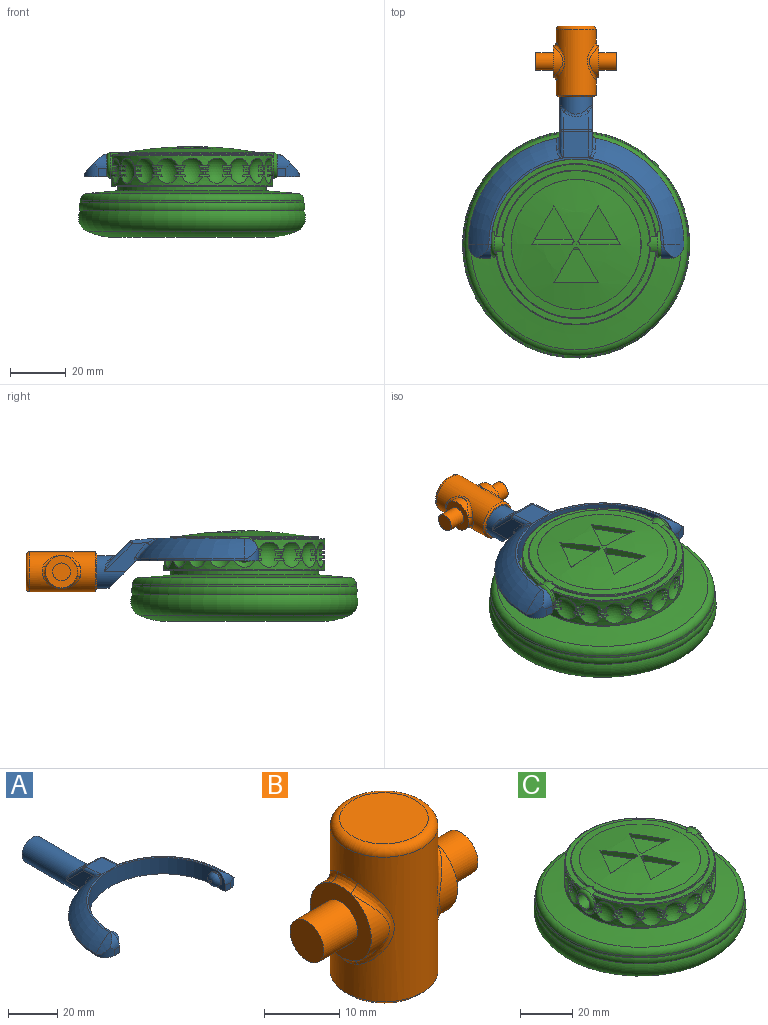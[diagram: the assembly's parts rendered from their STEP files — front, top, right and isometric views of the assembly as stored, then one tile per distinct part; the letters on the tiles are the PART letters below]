
ASSEMBLY  parts=3 mates=2
PART A: 48 faces, bbox 77.3x80.8x18.2 mm
  f0: plane 11.99x9.83mm, normal (0,-0.71,-0.71), area 141.5mm2, adj f1,f2,f9,f30,f43,f46
  f1: plane 15.39x10.49mm, normal (-1,0,0), area 63.5mm2, adj f0,f30,f32,f36,f46,f47
  f2: plane 15.39x10.49mm, normal (1,0,0), area 63.5mm2, adj f0,f30,f34,f39,f43,f44
  f3: plane 9.14x6.37mm, normal (0,0.71,0.71), area 67.6mm2, adj f35,f36,f39,f40
  f4: cylinder r=38.61mm len=37.99mm, axis (0,0,-1), area 42.6mm2, adj f6,f9,f17,f46,f47
  f5: torus R=19.3mm, axis (0,0,-1), area 507.8mm2, adj f10,f11,f12,f29,f42,f44
  f6: torus R=19.3mm, axis (0,0,-1), area 507.8mm2, adj f4,f11,f15,f28,f45,f47
  f7: cylinder r=30.48mm len=60.96mm, axis (0,0,-1), area 746.6mm2, adj f8,f9,f11,f14,f21,f24
  f8: plane 8.13x5.08mm, normal (-1,0,0), area 19.9mm2, adj f7,f9,f13,f19,f24
  f9: plane 77.22x43.73mm, normal (0,0,-1), area 956.2mm2, adj f0,f4,f7,f8,f10,f13,f14,f16
  f10: cylinder r=38.61mm len=37.99mm, axis (0,0,-1), area 42.6mm2, adj f5,f9,f20,f43,f44
  f11: plane 62.55x30.95mm, normal (0,0,1), area 75mm2, adj f5,f6,f7,f18,f19,f27
  f12: cylinder r=22.71mm len=7.33mm, axis (0,1,0), area 24.8mm2, adj f5,f19,f20
  f13: plane 3.05x3.05mm, normal (0,-1,0), area 9.3mm2, adj f8,f9,f19,f20
  f14: plane 8.13x5.08mm, normal (1,0,0), area 19.9mm2, adj f7,f9,f16,f18,f21
  f15: cylinder r=22.71mm len=7.33mm, axis (0,1,0), area 24.8mm2, adj f6,f17,f18
  f16: plane 3.05x3.05mm, normal (0,-1,0), area 9.3mm2, adj f9,f14,f17,f18
  f17: cylinder r=5.08mm len=5.08mm, axis (0,0,-1), area 21.9mm2, adj f4,f9,f15,f16,f18
  f18: cylinder r=5.08mm len=5.08mm, axis (-1,0,0), area 21.9mm2, adj f11,f14,f15,f16,f17
  f19: cylinder r=5.08mm len=5.08mm, axis (-1,0,0), area 21.9mm2, adj f8,f11,f12,f13,f20
  f20: cylinder r=5.08mm len=5.08mm, axis (0,0,-1), area 21.9mm2, adj f9,f10,f12,f13,f19
  f21: cylinder r=3.17mm len=6.35mm, axis (-1,0,0), area 12.7mm2, adj f7,f14,f23
  f22: plane 1.27x1.27mm, normal (1,0,0), area 1.3mm2, adj f23
  f23: torus R=0.64mm, axis (1,0,0), area 56.5mm2, adj f21,f22
  f24: cylinder r=3.17mm len=6.35mm, axis (1,0,0), area 12.7mm2, adj f7,f8,f26
  f25: plane 1.27x1.27mm, normal (-1,0,0), area 1.3mm2, adj f26
  f26: torus R=0.64mm, axis (-1,0,0), area 56.5mm2, adj f24,f25
  f27: plane 9.86x9.36mm, normal (0,0.09,1), area 85.6mm2, adj f11,f28,f29,f32,f34,f35,f42,f45
  f28: plane 1.04x0.17mm, normal (0,-1,0), area 0mm2, adj f6,f27,f45
  f29: plane 1.04x0.17mm, normal (0,-1,0), area 0mm2, adj f5,f27,f42
  f30: cylinder r=5.84mm len=33.01mm, axis (0,-1,0), area 1029.7mm2, adj f0,f1,f2,f31,f38,f40,f41
  f31: plane 11.68x11.68mm, normal (0,1,0), area 107.2mm2, adj f30
  f32: cylinder r=1.27mm len=9.13mm, axis (0,-1,0.09), area 14.4mm2, adj f1,f27,f33,f45
  f33: sphere r=1.27mm, area 1.5mm2, adj f32,f35,f36
  f34: cylinder r=1.27mm len=9.13mm, axis (0,1,-0.09), area 14.4mm2, adj f2,f27,f37,f42
  f35: cylinder r=1.27mm len=9.14mm, axis (-1,0,0), area 8.1mm2, adj f3,f27,f33,f37
  f36: cylinder r=1.27mm len=10.91mm, axis (0,-0.71,0.71), area 23.1mm2, adj f1,f3,f33,f38
  f37: sphere r=1.27mm, area 1.5mm2, adj f34,f35,f39
  f38: bspline ~4.55x2.75mm, area 2.3mm2, adj f30,f36,f40
  f39: cylinder r=1.27mm len=10.91mm, axis (0,0.71,-0.71), area 23.1mm2, adj f2,f3,f37,f41
  f40: bspline ~9.14x2.56mm, area 10.7mm2, adj f3,f30,f38,f41
  f41: bspline ~5.23x3.53mm, area 2.3mm2, adj f30,f39,f40
  f42: bspline ~4.62x3.14mm, area 5.2mm2, adj f5,f27,f29,f34,f44
  f43: cylinder r=1.27mm len=1.74mm, axis (0,0,-1), area 1.9mm2, adj f0,f2,f9,f10,f44
  f44: bspline ~8.6x7.86mm, area 11.9mm2, adj f2,f5,f10,f42,f43
  f45: bspline ~4.62x3.14mm, area 5.2mm2, adj f6,f27,f28,f32,f47
  f46: cylinder r=1.27mm len=1.74mm, axis (0,0,-1), area 1.9mm2, adj f0,f1,f4,f9,f47
  f47: bspline ~8.6x7.86mm, area 11.9mm2, adj f1,f4,f6,f45,f46
PART B: 25 faces, bbox 28.9x15.5x25.4 mm
  f0: cylinder r=5.71mm len=10.81mm, axis (-1,0,0), area 26.2mm2, adj f5,f15
  f1: cylinder r=5.71mm len=10.81mm, axis (-1,0,0), area 26.2mm2, adj f8,f11
  f2: cylinder r=7.14mm len=23.5mm, axis (0,0,-1), area 763.2mm2, adj f9,f10,f11,f12,f13,f14,f15,f16
  f3: plane 11.75x11.75mm, normal (0,0,1), area 108.4mm2, adj f17
  f4: plane 13.02x13.02mm, normal (0,0,-1), area 16.3mm2, adj f22,f24
  f5: plane 11.46x11.46mm, normal (1,0,0), area 70.9mm2, adj f0,f6,f13,f16,f18
  f6: cylinder r=5.71mm len=10.81mm, axis (-1,0,0), area 26.2mm2, adj f5,f14
  f7: cylinder r=5.71mm len=10.81mm, axis (-1,0,0), area 26.2mm2, adj f8,f10
  f8: plane 11.46x11.46mm, normal (-1,0,0), area 70.9mm2, adj f1,f7,f9,f12,f20
  f9: bspline ~4.64x1.73mm, area 6.5mm2, adj f2,f8,f10,f11
  f10: bspline ~13.62x4.91mm, area 20.7mm2, adj f2,f7,f9,f12
  f11: bspline ~13.6x4.87mm, area 20.7mm2, adj f1,f2,f9,f12
  f12: bspline ~4.64x1.73mm, area 6.5mm2, adj f2,f8,f10,f11
  f13: bspline ~4.64x1.73mm, area 6.5mm2, adj f2,f5,f14,f15
  f14: bspline ~13.62x4.91mm, area 20.7mm2, adj f2,f6,f13,f16
  f15: bspline ~13.6x4.87mm, area 20.7mm2, adj f0,f2,f13,f16
  f16: bspline ~4.64x1.73mm, area 6.5mm2, adj f2,f5,f14,f15
  f17: torus R=5.87mm, axis (0,0,1), area 83.8mm2, adj f2,f3
  f18: cylinder r=3.17mm len=6.35mm, axis (-1,0,0), area 126.7mm2, adj f5,f19
  f19: plane 6.35x6.35mm, normal (1,0,0), area 31.7mm2, adj f18
  f20: cylinder r=3.17mm len=6.35mm, axis (1,0,0), area 126.7mm2, adj f8,f21
  f21: plane 6.35x6.35mm, normal (-1,0,0), area 31.7mm2, adj f20
  f22: cylinder r=6.1mm len=22.86mm, axis (0,0,-1), area 875.6mm2, adj f4,f23
  f23: plane 12.19x12.19mm, normal (0,0,-1), area 116.7mm2, adj f22
  f24: cone r=7.14mm half-angle=45deg, axis (0,0,1), area 38.5mm2, adj f2,f4
PART C: 294 faces, bbox 96.3x96.3x32.5 mm
  f0: sphere r=5.62mm, area 0.7mm2, adj f45,f49,f106,f282
  f1: sphere r=5.62mm, area 15.9mm2, adj f39,f48,f125,f282
  f2: sphere r=5.62mm, area 0.7mm2, adj f36,f40,f105,f282
  f3: cylinder r=28.87mm len=57.43mm, axis (0,0,-1), area 156mm2, adj f34,f43,f71,f72,f73,f74,f75,f76
  f4: cylinder r=28.87mm len=57.43mm, axis (0,0,-1), area 156mm2, adj f31,f52,f62,f63,f64,f65,f66,f67
  f5: cylinder r=28.87mm len=0.95mm, axis (0,0,-1), area 0.4mm2, adj f17,f33,f79,f283
  f6: cylinder r=28.87mm len=0.95mm, axis (0,0,-1), area 0.4mm2, adj f35,f42,f71,f282
  f7: cylinder r=28.87mm len=0.95mm, axis (0,0,-1), area 0.4mm2, adj f44,f51,f70,f282
  f8: cylinder r=28.87mm len=0.95mm, axis (0,0,-1), area 0.4mm2, adj f21,f30,f62,f283
  f9: sphere r=5.62mm, area 0.7mm2, adj f18,f28,f96,f283
  f10: sphere r=5.62mm, area 15.9mm2, adj f24,f27,f125,f283
  f11: sphere r=5.62mm, area 0.7mm2, adj f20,f25,f115,f283
  f12: plane 56.98x25.96mm, normal (0,0,1), area 166.4mm2, adj f15,f282,f283,f288
  f13: plane 56.98x25.96mm, normal (0,0,1), area 166.4mm2, adj f14,f282,f283,f291
  f14: cylinder r=26.57mm len=53.04mm, axis (0,0,-1), area 43.8mm2, adj f13,f282,f283,f292
  f15: cylinder r=26.57mm len=53.04mm, axis (0,0,-1), area 43.8mm2, adj f12,f282,f283,f289
  f16: cone r=26.57mm half-angle=87deg, axis (0,0,-1), area 474.1mm2, adj f282,f283,f289,f292,f293
  f17: plane 1.55x1.41mm, normal (0,0,-1), area 1.2mm2, adj f5,f19,f79,f283
  f18: plane 1.71x1.55mm, normal (0,0,1), area 1.5mm2, adj f9,f19,f79,f96,f283
  f19: cylinder r=27.6mm len=1.71mm, axis (0,0,-1), area 1mm2, adj f17,f18,f79,f283
  f20: plane 1.71x1.55mm, normal (0,0,1), area 1.5mm2, adj f11,f22,f62,f115,f283
  f21: plane 1.55x1.41mm, normal (0,0,-1), area 1.2mm2, adj f8,f22,f62,f283
  f22: cylinder r=27.6mm len=1.71mm, axis (0,0,-1), area 1mm2, adj f20,f21,f62,f283
  f23: cylinder r=27.6mm len=3.74mm, axis (0,0,-1), area 2.1mm2, adj f24,f25,f62,f283
  f24: plane 3.74x1.73mm, normal (0,0,1), area 3.1mm2, adj f10,f23,f62,f125,f283
  f25: plane 2.64x1.63mm, normal (0,0,-1), area 2.3mm2, adj f11,f23,f62,f115,f283
  f26: cylinder r=27.6mm len=3.74mm, axis (0,0,-1), area 2.1mm2, adj f27,f28,f79,f283
  f27: plane 3.74x1.73mm, normal (0,0,1), area 3.1mm2, adj f10,f26,f79,f125,f283
  f28: plane 2.64x1.63mm, normal (0,0,-1), area 2.3mm2, adj f9,f26,f79,f96,f283
  f29: cylinder r=27.6mm len=1.73mm, axis (0,0,-1), area 1mm2, adj f30,f31,f62,f283
  f30: plane 1.56x1.4mm, normal (0,0,1), area 1.1mm2, adj f8,f29,f62,f283
  f31: plane 1.68x1.62mm, normal (0,0,-1), area 1.4mm2, adj f4,f29,f62,f283
  f32: cylinder r=27.6mm len=1.73mm, axis (0,0,-1), area 1mm2, adj f33,f34,f79,f283
  f33: plane 1.56x1.4mm, normal (0,0,1), area 1.1mm2, adj f5,f32,f79,f283
  f34: plane 1.68x1.62mm, normal (0,0,-1), area 1.4mm2, adj f3,f32,f79,f283
  f35: plane 1.55x1.41mm, normal (0,0,-1), area 1.2mm2, adj f6,f37,f71,f282
  f36: plane 1.71x1.55mm, normal (0,0,1), area 1.5mm2, adj f2,f37,f71,f105,f282
  f37: cylinder r=27.6mm len=1.71mm, axis (0,0,-1), area 1mm2, adj f35,f36,f71,f282
  f38: cylinder r=27.6mm len=3.74mm, axis (0,0,-1), area 2.1mm2, adj f39,f40,f71,f282
  f39: plane 3.74x1.73mm, normal (0,0,1), area 3.1mm2, adj f1,f38,f71,f125,f282
  f40: plane 2.64x1.63mm, normal (0,0,-1), area 2.3mm2, adj f2,f38,f71,f105,f282
  f41: cylinder r=27.6mm len=1.73mm, axis (0,0,-1), area 1mm2, adj f42,f43,f71,f282
  f42: plane 1.56x1.4mm, normal (0,0,1), area 1.1mm2, adj f6,f41,f71,f282
  f43: plane 1.68x1.62mm, normal (0,0,-1), area 1.4mm2, adj f3,f41,f71,f282
  f44: plane 1.55x1.41mm, normal (0,0,-1), area 1.2mm2, adj f7,f46,f70,f282
  f45: plane 1.71x1.55mm, normal (0,0,1), area 1.5mm2, adj f0,f46,f70,f106,f282
  f46: cylinder r=27.6mm len=1.71mm, axis (0,0,-1), area 1mm2, adj f44,f45,f70,f282
  f47: cylinder r=27.6mm len=3.74mm, axis (0,0,-1), area 2.1mm2, adj f48,f49,f70,f282
  f48: plane 3.74x1.73mm, normal (0,0,1), area 3.1mm2, adj f1,f47,f70,f125,f282
  f49: plane 2.64x1.63mm, normal (0,0,-1), area 2.3mm2, adj f0,f47,f70,f106,f282
  f50: cylinder r=27.6mm len=1.73mm, axis (0,0,-1), area 1mm2, adj f51,f52,f70,f282
  f51: plane 1.56x1.4mm, normal (0,0,1), area 1.1mm2, adj f7,f50,f70,f282
  f52: plane 1.68x1.62mm, normal (0,0,-1), area 1.4mm2, adj f4,f50,f70,f282
  f53: cylinder r=1.27mm len=2.26mm, axis (0,0,1), area 2.9mm2, adj f54,f61,f272,f280
  f54: plane 14.61x2.12mm, normal (0,1,0), area 26.2mm2, adj f53,f61,f271,f280
  f55: plane 13.69x11.86mm, normal (0,0,1), area 81.2mm2, adj f271,f272,f280
  f56: plane 14.61x2.12mm, normal (0,1,0), area 26.2mm2, adj f57,f61,f274,f279
  f57: cylinder r=1.27mm len=2.26mm, axis (0,0,1), area 2.9mm2, adj f56,f61,f273,f279
  f58: plane 13.69x11.86mm, normal (0,0,1), area 81.2mm2, adj f273,f274,f279
  f59: cylinder r=1.27mm len=2.26mm, axis (0,0,1), area 3mm2, adj f61,f276,f277,f278
  f60: plane 15.88x11.86mm, normal (0,0,1), area 107.1mm2, adj f275,f276,f277,f278
  f61: sphere r=135.39mm, area 1385.3mm2, adj f53,f54,f56,f57,f59,f271,f272,f273
  f62: sphere r=5.62mm, area 66.8mm2, adj f4,f8,f20,f21,f22,f23,f24,f25
  f63: sphere r=5.62mm, area 66.8mm2, adj f4,f94,f95,f113,f114,f125,f253,f254
  f64: sphere r=5.62mm, area 66.8mm2, adj f4,f93,f94,f112,f113,f125,f244,f245
  f65: sphere r=5.62mm, area 66.8mm2, adj f4,f92,f93,f111,f112,f125,f235,f236
  f66: sphere r=5.62mm, area 66.8mm2, adj f4,f91,f92,f110,f111,f125,f226,f227
  f67: sphere r=5.62mm, area 66.8mm2, adj f4,f90,f91,f109,f110,f125,f217,f218
  f68: sphere r=5.62mm, area 66.8mm2, adj f4,f89,f90,f108,f109,f125,f208,f209
  f69: sphere r=5.62mm, area 66.8mm2, adj f4,f88,f89,f107,f108,f125,f199,f200
  f70: sphere r=5.62mm, area 66.8mm2, adj f4,f7,f44,f45,f46,f47,f48,f49
  f71: sphere r=5.62mm, area 66.8mm2, adj f3,f6,f35,f36,f37,f38,f39,f40
  f72: sphere r=5.62mm, area 66.8mm2, adj f3,f86,f87,f103,f104,f125,f181,f182
  f73: sphere r=5.62mm, area 66.8mm2, adj f3,f85,f86,f102,f103,f125,f172,f173
  f74: sphere r=5.62mm, area 66.8mm2, adj f3,f84,f85,f101,f102,f125,f163,f164
  f75: sphere r=5.62mm, area 66.8mm2, adj f3,f83,f84,f100,f101,f125,f154,f155
  f76: sphere r=5.62mm, area 66.8mm2, adj f3,f82,f83,f99,f100,f125,f145,f146
  f77: sphere r=5.62mm, area 66.8mm2, adj f3,f81,f82,f98,f99,f125,f136,f137
  f78: sphere r=5.62mm, area 66.8mm2, adj f3,f80,f81,f97,f98,f125,f127,f128
  f79: sphere r=5.62mm, area 66.8mm2, adj f3,f5,f17,f18,f19,f26,f27,f28
  f80: cylinder r=28.87mm len=0.95mm, axis (0,0,-1), area 0.7mm2, adj f78,f79,f127,f134
  f81: cylinder r=28.87mm len=0.95mm, axis (0,0,-1), area 0.7mm2, adj f77,f78,f136,f143
  f82: cylinder r=28.87mm len=0.95mm, axis (0,0,-1), area 0.7mm2, adj f76,f77,f145,f152
  f83: cylinder r=28.87mm len=0.95mm, axis (0,0,-1), area 0.7mm2, adj f75,f76,f154,f161
  f84: cylinder r=28.87mm len=0.95mm, axis (0,0,-1), area 0.7mm2, adj f74,f75,f163,f170
  f85: cylinder r=28.87mm len=0.95mm, axis (0,0,-1), area 0.7mm2, adj f73,f74,f172,f179
  f86: cylinder r=28.87mm len=0.95mm, axis (0,0,-1), area 0.7mm2, adj f72,f73,f181,f188
  f87: cylinder r=28.87mm len=0.95mm, axis (0,0,-1), area 0.7mm2, adj f71,f72,f190,f197
  f88: cylinder r=28.87mm len=0.95mm, axis (0,0,-1), area 0.7mm2, adj f69,f70,f199,f206
  f89: cylinder r=28.87mm len=0.95mm, axis (0,0,-1), area 0.7mm2, adj f68,f69,f208,f215
  f90: cylinder r=28.87mm len=0.95mm, axis (0,0,-1), area 0.7mm2, adj f67,f68,f217,f224
  f91: cylinder r=28.87mm len=0.95mm, axis (0,0,-1), area 0.7mm2, adj f66,f67,f226,f233
  f92: cylinder r=28.87mm len=0.95mm, axis (0,0,-1), area 0.7mm2, adj f65,f66,f235,f242
  f93: cylinder r=28.87mm len=0.95mm, axis (0,0,-1), area 0.7mm2, adj f64,f65,f244,f251
  f94: cylinder r=28.87mm len=0.95mm, axis (0,0,-1), area 0.7mm2, adj f63,f64,f253,f260
  f95: cylinder r=28.87mm len=0.95mm, axis (0,0,-1), area 0.7mm2, adj f62,f63,f263,f269
  f96: cylinder r=28.87mm len=0.95mm, axis (0,0,-1), area 0.7mm2, adj f9,f18,f28,f79
  f97: cylinder r=28.87mm len=0.95mm, axis (0,0,-1), area 0.7mm2, adj f78,f79,f128,f132
  f98: cylinder r=28.87mm len=0.95mm, axis (0,0,-1), area 0.7mm2, adj f77,f78,f137,f141
  f99: cylinder r=28.87mm len=0.95mm, axis (0,0,-1), area 0.7mm2, adj f76,f77,f146,f150
  f100: cylinder r=28.87mm len=0.95mm, axis (0,0,-1), area 0.7mm2, adj f75,f76,f155,f159
  f101: cylinder r=28.87mm len=0.95mm, axis (0,0,-1), area 0.7mm2, adj f74,f75,f164,f168
  f102: cylinder r=28.87mm len=0.95mm, axis (0,0,-1), area 0.7mm2, adj f73,f74,f173,f177
  f103: cylinder r=28.87mm len=0.95mm, axis (0,0,-1), area 0.7mm2, adj f72,f73,f182,f186
  f104: cylinder r=28.87mm len=0.95mm, axis (0,0,-1), area 0.7mm2, adj f71,f72,f191,f195
  f105: cylinder r=28.87mm len=0.95mm, axis (0,0,-1), area 0.7mm2, adj f2,f36,f40,f71
  f106: cylinder r=28.87mm len=0.95mm, axis (0,0,-1), area 0.7mm2, adj f0,f45,f49,f70
  f107: cylinder r=28.87mm len=0.95mm, axis (0,0,-1), area 0.7mm2, adj f69,f70,f200,f204
  f108: cylinder r=28.87mm len=0.95mm, axis (0,0,-1), area 0.7mm2, adj f68,f69,f209,f213
  f109: cylinder r=28.87mm len=0.95mm, axis (0,0,-1), area 0.7mm2, adj f67,f68,f218,f222
  f110: cylinder r=28.87mm len=0.95mm, axis (0,0,-1), area 0.7mm2, adj f66,f67,f227,f231
  f111: cylinder r=28.87mm len=0.95mm, axis (0,0,-1), area 0.7mm2, adj f65,f66,f236,f240
  f112: cylinder r=28.87mm len=0.95mm, axis (0,0,-1), area 0.7mm2, adj f64,f65,f245,f249
  f113: cylinder r=28.87mm len=0.95mm, axis (0,0,-1), area 0.7mm2, adj f63,f64,f254,f258
  f114: cylinder r=28.87mm len=0.95mm, axis (0,0,-1), area 0.7mm2, adj f62,f63,f264,f265
  f115: cylinder r=28.87mm len=0.95mm, axis (0,0,-1), area 0.7mm2, adj f11,f20,f25,f62
  f116: plane 39.33x39.33mm, normal (0,0,-1), area 1214.6mm2, adj f117
  f117: torus R=20.12mm, axis (0,0,-1), area 1429.3mm2, adj f116,f118
  f118: torus R=27.74mm, axis (0,0,-1), area 3542.1mm2, adj f117,f119
  f119: torus R=35.36mm, axis (0,0,-1), area 2180.1mm2, adj f118,f120
  f120: torus R=37.35mm, axis (0,0,-1), area 734.6mm2, adj f119,f121
  f121: cylinder r=40.06mm len=80.11mm, axis (0,0,-1), area 213.3mm2, adj f120,f126
  f122: cone r=26.57mm half-angle=85deg, axis (0,0,-1), area 2265mm2, adj f123,f126
  f123: cylinder r=26.57mm len=53.14mm, axis (0,0,-1), area 265mm2, adj f122,f124
  f124: plane 57.23x57.23mm, normal (0,0,-1), area 354.5mm2, adj f123,f290
  f125: cylinder r=28.87mm len=57.73mm, axis (0,0,-1), area 339.8mm2, adj f1,f10,f24,f27,f39,f48,f62,f63
  f126: torus R=37.52mm, axis (0,0,1), area 928.6mm2, adj f121,f122
  f127: plane 2.51x1.93mm, normal (0,0,-1), area 2mm2, adj f78,f79,f80,f129
  f128: plane 2.51x1.93mm, normal (0,0,1), area 2mm2, adj f78,f79,f97,f129
  f129: cylinder r=27.6mm len=2.51mm, axis (0,0,-1), area 1.8mm2, adj f78,f79,f127,f128
  f130: cylinder r=27.6mm len=3.53mm, axis (0,0,-1), area 2.3mm2, adj f78,f79,f131,f132
  f131: plane 3.53x2.4mm, normal (0,0,1), area 3.2mm2, adj f78,f79,f125,f130
  f132: plane 2.92x2.12mm, normal (0,0,-1), area 2.5mm2, adj f78,f79,f97,f130
  f133: cylinder r=27.6mm len=3.52mm, axis (0,0,-1), area 2.3mm2, adj f78,f79,f134,f135
  f134: plane 2.91x2.12mm, normal (0,0,1), area 2.5mm2, adj f78,f79,f80,f133
  f135: plane 3.52x2.39mm, normal (0,0,-1), area 3.1mm2, adj f3,f78,f79,f133
  f136: plane 2.12x2.12mm, normal (0,0,-1), area 2mm2, adj f77,f78,f81,f138
  f137: plane 2.12x2.12mm, normal (0,0,1), area 2mm2, adj f77,f78,f98,f138
  f138: cylinder r=27.6mm len=1.99mm, axis (0,0,-1), area 1.8mm2, adj f77,f78,f136,f137
  f139: cylinder r=27.6mm len=2.81mm, axis (0,0,-1), area 2.3mm2, adj f77,f78,f140,f141
  f140: plane 2.82x2.82mm, normal (0,0,1), area 3.2mm2, adj f77,f78,f125,f139
  f141: plane 2.41x2.41mm, normal (0,0,-1), area 2.5mm2, adj f77,f78,f98,f139
  f142: cylinder r=27.6mm len=2.79mm, axis (0,0,-1), area 2.3mm2, adj f77,f78,f143,f144
  f143: plane 2.4x2.4mm, normal (0,0,1), area 2.5mm2, adj f77,f78,f81,f142
  f144: plane 2.81x2.81mm, normal (0,0,-1), area 3.1mm2, adj f3,f77,f78,f142
  f145: plane 2.51x1.93mm, normal (0,0,-1), area 2mm2, adj f76,f77,f82,f147
  f146: plane 2.51x1.93mm, normal (0,0,1), area 2mm2, adj f76,f77,f99,f147
  f147: cylinder r=27.6mm len=2.51mm, axis (0,0,-1), area 1.8mm2, adj f76,f77,f145,f146
  f148: cylinder r=27.6mm len=3.53mm, axis (0,0,-1), area 2.3mm2, adj f76,f77,f149,f150
  f149: plane 3.53x2.4mm, normal (0,0,1), area 3.2mm2, adj f76,f77,f125,f148
  f150: plane 2.92x2.12mm, normal (0,0,-1), area 2.5mm2, adj f76,f77,f99,f148
  f151: cylinder r=27.6mm len=3.52mm, axis (0,0,-1), area 2.3mm2, adj f76,f77,f152,f153
  f152: plane 2.91x2.12mm, normal (0,0,1), area 2.5mm2, adj f76,f77,f82,f151
  f153: plane 3.52x2.39mm, normal (0,0,-1), area 3.1mm2, adj f3,f76,f77,f151
  f154: plane 2.78x1.55mm, normal (0,0,-1), area 2mm2, adj f75,f76,f83,f156
  f155: plane 2.78x1.55mm, normal (0,0,1), area 2mm2, adj f75,f76,f100,f156
  f156: cylinder r=27.6mm len=2.78mm, axis (0,0,-1), area 1.8mm2, adj f75,f76,f154,f155
  f157: cylinder r=27.6mm len=3.92mm, axis (0,0,-1), area 2.3mm2, adj f75,f76,f158,f159
  f158: plane 3.92x1.73mm, normal (0,0,1), area 3.2mm2, adj f75,f76,f125,f157
  f159: plane 3.24x1.63mm, normal (0,0,-1), area 2.5mm2, adj f75,f76,f100,f157
  f160: cylinder r=27.6mm len=3.9mm, axis (0,0,-1), area 2.3mm2, adj f75,f76,f161,f162
  f161: plane 3.23x1.62mm, normal (0,0,1), area 2.5mm2, adj f75,f76,f83,f160
  f162: plane 3.9x1.73mm, normal (0,0,-1), area 3.1mm2, adj f3,f75,f76,f160
  f163: plane 2.78x1.55mm, normal (0,0,-1), area 2mm2, adj f74,f75,f84,f165
  f164: plane 2.78x1.55mm, normal (0,0,1), area 2mm2, adj f74,f75,f101,f165
  f165: cylinder r=27.6mm len=2.78mm, axis (0,0,-1), area 1.8mm2, adj f74,f75,f163,f164
  f166: cylinder r=27.6mm len=3.92mm, axis (0,0,-1), area 2.3mm2, adj f74,f75,f167,f168
  f167: plane 3.92x1.73mm, normal (0,0,1), area 3.2mm2, adj f74,f75,f125,f166
  f168: plane 3.24x1.63mm, normal (0,0,-1), area 2.5mm2, adj f74,f75,f101,f166
  f169: cylinder r=27.6mm len=3.9mm, axis (0,0,-1), area 2.3mm2, adj f74,f75,f170,f171
  f170: plane 3.23x1.62mm, normal (0,0,1), area 2.5mm2, adj f74,f75,f84,f169
  f171: plane 3.9x1.73mm, normal (0,0,-1), area 3.1mm2, adj f3,f74,f75,f169
  f172: plane 2.51x1.93mm, normal (0,0,-1), area 2mm2, adj f73,f74,f85,f174
  f173: plane 2.51x1.93mm, normal (0,0,1), area 2mm2, adj f73,f74,f102,f174
  f174: cylinder r=27.6mm len=2.51mm, axis (0,0,-1), area 1.8mm2, adj f73,f74,f172,f173
  f175: cylinder r=27.6mm len=3.53mm, axis (0,0,-1), area 2.3mm2, adj f73,f74,f176,f177
  f176: plane 3.53x2.4mm, normal (0,0,1), area 3.2mm2, adj f73,f74,f125,f175
  f177: plane 2.92x2.12mm, normal (0,0,-1), area 2.5mm2, adj f73,f74,f102,f175
  f178: cylinder r=27.6mm len=3.52mm, axis (0,0,-1), area 2.3mm2, adj f73,f74,f179,f180
  f179: plane 2.91x2.12mm, normal (0,0,1), area 2.5mm2, adj f73,f74,f85,f178
  f180: plane 3.52x2.39mm, normal (0,0,-1), area 3.1mm2, adj f3,f73,f74,f178
  f181: plane 2.12x2.12mm, normal (0,0,-1), area 2mm2, adj f72,f73,f86,f183
  f182: plane 2.12x2.12mm, normal (0,0,1), area 2mm2, adj f72,f73,f103,f183
  f183: cylinder r=27.6mm len=1.99mm, axis (0,0,-1), area 1.8mm2, adj f72,f73,f181,f182
  f184: cylinder r=27.6mm len=2.81mm, axis (0,0,-1), area 2.3mm2, adj f72,f73,f185,f186
  f185: plane 2.82x2.82mm, normal (0,0,1), area 3.2mm2, adj f72,f73,f125,f184
  f186: plane 2.41x2.41mm, normal (0,0,-1), area 2.5mm2, adj f72,f73,f103,f184
  f187: cylinder r=27.6mm len=2.79mm, axis (0,0,-1), area 2.3mm2, adj f72,f73,f188,f189
  f188: plane 2.4x2.4mm, normal (0,0,1), area 2.5mm2, adj f72,f73,f86,f187
  f189: plane 2.81x2.81mm, normal (0,0,-1), area 3.1mm2, adj f3,f72,f73,f187
  f190: plane 2.51x1.93mm, normal (0,0,-1), area 2mm2, adj f71,f72,f87,f192
  f191: plane 2.51x1.93mm, normal (0,0,1), area 2mm2, adj f71,f72,f104,f192
  f192: cylinder r=27.6mm len=2.51mm, axis (0,0,-1), area 1.8mm2, adj f71,f72,f190,f191
  f193: cylinder r=27.6mm len=3.53mm, axis (0,0,-1), area 2.3mm2, adj f71,f72,f194,f195
  f194: plane 3.53x2.4mm, normal (0,0,1), area 3.2mm2, adj f71,f72,f125,f193
  f195: plane 2.92x2.12mm, normal (0,0,-1), area 2.5mm2, adj f71,f72,f104,f193
  f196: cylinder r=27.6mm len=3.52mm, axis (0,0,-1), area 2.3mm2, adj f71,f72,f197,f198
  f197: plane 2.91x2.12mm, normal (0,0,1), area 2.5mm2, adj f71,f72,f87,f196
  f198: plane 3.52x2.39mm, normal (0,0,-1), area 3.1mm2, adj f3,f71,f72,f196
  f199: plane 2.51x1.93mm, normal (0,0,-1), area 2mm2, adj f69,f70,f88,f201
  f200: plane 2.51x1.93mm, normal (0,0,1), area 2mm2, adj f69,f70,f107,f201
  f201: cylinder r=27.6mm len=2.51mm, axis (0,0,-1), area 1.8mm2, adj f69,f70,f199,f200
  f202: cylinder r=27.6mm len=3.53mm, axis (0,0,-1), area 2.3mm2, adj f69,f70,f203,f204
  f203: plane 3.53x2.4mm, normal (0,0,1), area 3.2mm2, adj f69,f70,f125,f202
  f204: plane 2.92x2.12mm, normal (0,0,-1), area 2.5mm2, adj f69,f70,f107,f202
  f205: cylinder r=27.6mm len=3.52mm, axis (0,0,-1), area 2.3mm2, adj f69,f70,f206,f207
  f206: plane 2.91x2.12mm, normal (0,0,1), area 2.5mm2, adj f69,f70,f88,f205
  f207: plane 3.52x2.39mm, normal (0,0,-1), area 3.1mm2, adj f4,f69,f70,f205
  f208: plane 2.12x2.12mm, normal (0,0,-1), area 2mm2, adj f68,f69,f89,f210
  f209: plane 2.12x2.12mm, normal (0,0,1), area 2mm2, adj f68,f69,f108,f210
  f210: cylinder r=27.6mm len=1.99mm, axis (0,0,-1), area 1.8mm2, adj f68,f69,f208,f209
  f211: cylinder r=27.6mm len=2.81mm, axis (0,0,-1), area 2.3mm2, adj f68,f69,f212,f213
  f212: plane 2.82x2.82mm, normal (0,0,1), area 3.2mm2, adj f68,f69,f125,f211
  f213: plane 2.41x2.41mm, normal (0,0,-1), area 2.5mm2, adj f68,f69,f108,f211
  f214: cylinder r=27.6mm len=2.79mm, axis (0,0,-1), area 2.3mm2, adj f68,f69,f215,f216
  f215: plane 2.4x2.4mm, normal (0,0,1), area 2.5mm2, adj f68,f69,f89,f214
  f216: plane 2.81x2.81mm, normal (0,0,-1), area 3.1mm2, adj f4,f68,f69,f214
  f217: plane 2.51x1.93mm, normal (0,0,-1), area 2mm2, adj f67,f68,f90,f219
  f218: plane 2.51x1.93mm, normal (0,0,1), area 2mm2, adj f67,f68,f109,f219
  f219: cylinder r=27.6mm len=2.51mm, axis (0,0,-1), area 1.8mm2, adj f67,f68,f217,f218
  f220: cylinder r=27.6mm len=3.53mm, axis (0,0,-1), area 2.3mm2, adj f67,f68,f221,f222
  f221: plane 3.53x2.4mm, normal (0,0,1), area 3.2mm2, adj f67,f68,f125,f220
  f222: plane 2.92x2.12mm, normal (0,0,-1), area 2.5mm2, adj f67,f68,f109,f220
  f223: cylinder r=27.6mm len=3.52mm, axis (0,0,-1), area 2.3mm2, adj f67,f68,f224,f225
  f224: plane 2.91x2.12mm, normal (0,0,1), area 2.5mm2, adj f67,f68,f90,f223
  f225: plane 3.52x2.39mm, normal (0,0,-1), area 3.1mm2, adj f4,f67,f68,f223
  f226: plane 2.78x1.55mm, normal (0,0,-1), area 2mm2, adj f66,f67,f91,f228
  f227: plane 2.78x1.55mm, normal (0,0,1), area 2mm2, adj f66,f67,f110,f228
  f228: cylinder r=27.6mm len=2.78mm, axis (0,0,-1), area 1.8mm2, adj f66,f67,f226,f227
  f229: cylinder r=27.6mm len=3.92mm, axis (0,0,-1), area 2.3mm2, adj f66,f67,f230,f231
  f230: plane 3.92x1.73mm, normal (0,0,1), area 3.2mm2, adj f66,f67,f125,f229
  f231: plane 3.24x1.63mm, normal (0,0,-1), area 2.5mm2, adj f66,f67,f110,f229
  f232: cylinder r=27.6mm len=3.9mm, axis (0,0,-1), area 2.3mm2, adj f66,f67,f233,f234
  f233: plane 3.23x1.62mm, normal (0,0,1), area 2.5mm2, adj f66,f67,f91,f232
  f234: plane 3.9x1.73mm, normal (0,0,-1), area 3.1mm2, adj f4,f66,f67,f232
  f235: plane 2.78x1.55mm, normal (0,0,-1), area 2mm2, adj f65,f66,f92,f237
  f236: plane 2.78x1.55mm, normal (0,0,1), area 2mm2, adj f65,f66,f111,f237
  f237: cylinder r=27.6mm len=2.78mm, axis (0,0,-1), area 1.8mm2, adj f65,f66,f235,f236
  f238: cylinder r=27.6mm len=3.92mm, axis (0,0,-1), area 2.3mm2, adj f65,f66,f239,f240
  f239: plane 3.92x1.73mm, normal (0,0,1), area 3.2mm2, adj f65,f66,f125,f238
  f240: plane 3.24x1.63mm, normal (0,0,-1), area 2.5mm2, adj f65,f66,f111,f238
  f241: cylinder r=27.6mm len=3.9mm, axis (0,0,-1), area 2.3mm2, adj f65,f66,f242,f243
  f242: plane 3.23x1.62mm, normal (0,0,1), area 2.5mm2, adj f65,f66,f92,f241
  f243: plane 3.9x1.73mm, normal (0,0,-1), area 3.1mm2, adj f4,f65,f66,f241
  f244: plane 2.51x1.93mm, normal (0,0,-1), area 2mm2, adj f64,f65,f93,f246
  f245: plane 2.51x1.93mm, normal (0,0,1), area 2mm2, adj f64,f65,f112,f246
  f246: cylinder r=27.6mm len=2.51mm, axis (0,0,-1), area 1.8mm2, adj f64,f65,f244,f245
  f247: cylinder r=27.6mm len=3.53mm, axis (0,0,-1), area 2.3mm2, adj f64,f65,f248,f249
  f248: plane 3.53x2.4mm, normal (0,0,1), area 3.2mm2, adj f64,f65,f125,f247
  f249: plane 2.92x2.12mm, normal (0,0,-1), area 2.5mm2, adj f64,f65,f112,f247
  f250: cylinder r=27.6mm len=3.52mm, axis (0,0,-1), area 2.3mm2, adj f64,f65,f251,f252
  f251: plane 2.91x2.12mm, normal (0,0,1), area 2.5mm2, adj f64,f65,f93,f250
  f252: plane 3.52x2.39mm, normal (0,0,-1), area 3.1mm2, adj f4,f64,f65,f250
  f253: plane 2.12x2.12mm, normal (0,0,-1), area 2mm2, adj f63,f64,f94,f255
  f254: plane 2.12x2.12mm, normal (0,0,1), area 2mm2, adj f63,f64,f113,f255
  f255: cylinder r=27.6mm len=1.99mm, axis (0,0,-1), area 1.8mm2, adj f63,f64,f253,f254
  f256: cylinder r=27.6mm len=2.81mm, axis (0,0,-1), area 2.3mm2, adj f63,f64,f257,f258
  f257: plane 2.82x2.82mm, normal (0,0,1), area 3.2mm2, adj f63,f64,f125,f256
  f258: plane 2.41x2.41mm, normal (0,0,-1), area 2.5mm2, adj f63,f64,f113,f256
  f259: cylinder r=27.6mm len=2.79mm, axis (0,0,-1), area 2.3mm2, adj f63,f64,f260,f261
  f260: plane 2.4x2.4mm, normal (0,0,1), area 2.5mm2, adj f63,f64,f94,f259
  f261: plane 2.81x2.81mm, normal (0,0,-1), area 3.1mm2, adj f4,f63,f64,f259
  f262: cylinder r=27.6mm len=2.51mm, axis (0,0,-1), area 1.8mm2, adj f62,f63,f263,f264
  f263: plane 2.51x1.93mm, normal (0,0,-1), area 2mm2, adj f62,f63,f95,f262
  f264: plane 2.51x1.93mm, normal (0,0,1), area 2mm2, adj f62,f63,f114,f262
  f265: plane 2.92x2.12mm, normal (0,0,-1), area 2.5mm2, adj f62,f63,f114,f267
  f266: plane 3.53x2.4mm, normal (0,0,1), area 3.2mm2, adj f62,f63,f125,f267
  f267: cylinder r=27.6mm len=3.53mm, axis (0,0,-1), area 2.3mm2, adj f62,f63,f265,f266
  f268: plane 3.52x2.39mm, normal (0,0,-1), area 3.1mm2, adj f4,f62,f63,f270
  f269: plane 2.91x2.12mm, normal (0,0,1), area 2.5mm2, adj f62,f63,f95,f270
  f270: cylinder r=27.6mm len=3.52mm, axis (0,0,-1), area 2.3mm2, adj f62,f63,f268,f269
  f271: plane 13.77x7.96mm, normal (-0.87,-0.5,0), area 27.4mm2, adj f54,f55,f61,f272,f280
  f272: plane 12.66x7.31mm, normal (0.87,-0.5,0), area 32mm2, adj f53,f55,f61,f271,f280
  f273: plane 12.66x7.31mm, normal (-0.87,-0.5,0), area 32mm2, adj f57,f58,f61,f274,f279
  f274: plane 13.77x7.96mm, normal (0.87,-0.5,0), area 27.4mm2, adj f56,f58,f61,f273,f279
  f275: plane 15.88x1.84mm, normal (0,1,0), area 28mm2, adj f60,f61,f276,f277
  f276: plane 12.66x7.31mm, normal (-0.87,-0.5,0), area 32mm2, adj f59,f60,f61,f275,f278
  f277: plane 12.66x7.31mm, normal (0.87,-0.5,0), area 32mm2, adj f59,f60,f61,f275,f278
  f278: cylinder r=4.57mm len=2.19mm, axis (-1,0,0), area 1.3mm2, adj f59,f60,f276,f277
  f279: cylinder r=4.57mm len=15.24mm, axis (-1,0,0), area 28mm2, adj f56,f57,f58,f273,f274
  f280: cylinder r=4.57mm len=15.24mm, axis (-1,0,0), area 28mm2, adj f53,f54,f55,f271,f272
  f281: plane 6.6x6.6mm, normal (1,0,0), area 2.6mm2, adj f286,f287
  f282: cylinder r=4.57mm len=9.14mm, axis (-1,0,0), area 44.1mm2, adj f0,f1,f2,f3,f4,f6,f7,f12
  f283: cylinder r=4.57mm len=9.14mm, axis (-1,0,0), area 44.1mm2, adj f3,f4,f5,f8,f9,f10,f11,f12
  f284: plane 6.6x6.6mm, normal (-1,0,0), area 2.6mm2, adj f285,f287
  f285: torus R=3.3mm, axis (1,0,0), area 51.5mm2, adj f283,f284
  f286: torus R=3.3mm, axis (1,0,0), area 51.5mm2, adj f281,f282
  f287: cylinder r=3.17mm len=60.96mm, axis (1,0,0), area 1216.1mm2, adj f281,f284
  f288: torus R=28.61mm, axis (0,0,-1), area 33.8mm2, adj f4,f12,f282,f283
  f289: torus R=26.31mm, axis (0,0,1), area 31.2mm2, adj f15,f16,f282,f283
  f290: torus R=28.61mm, axis (0,0,1), area 72.1mm2, adj f124,f125
  f291: torus R=28.61mm, axis (0,0,-1), area 33.8mm2, adj f3,f13,f282,f283
  f292: torus R=26.31mm, axis (0,0,1), area 31.2mm2, adj f14,f16,f282,f283
  f293: torus R=23.29mm, axis (0,0,1), area 4.5mm2, adj f16,f61
PLACE A t=(32.34,27.52,20.85)mm
PLACE B rot(axis=(-1,0,0),90deg) t=(32.34,80.3,16.88)mm
PLACE C t=(32.34,27.52,31.62)mm
MATE revolute A.f24 <-> C.f278  axis (-1,0,0) through (62.82,27.52,24.92)mm
MATE revolute B.f2 <-> A.f30  axis (0,-1,0) through (32.34,103.16,16.88)mm
